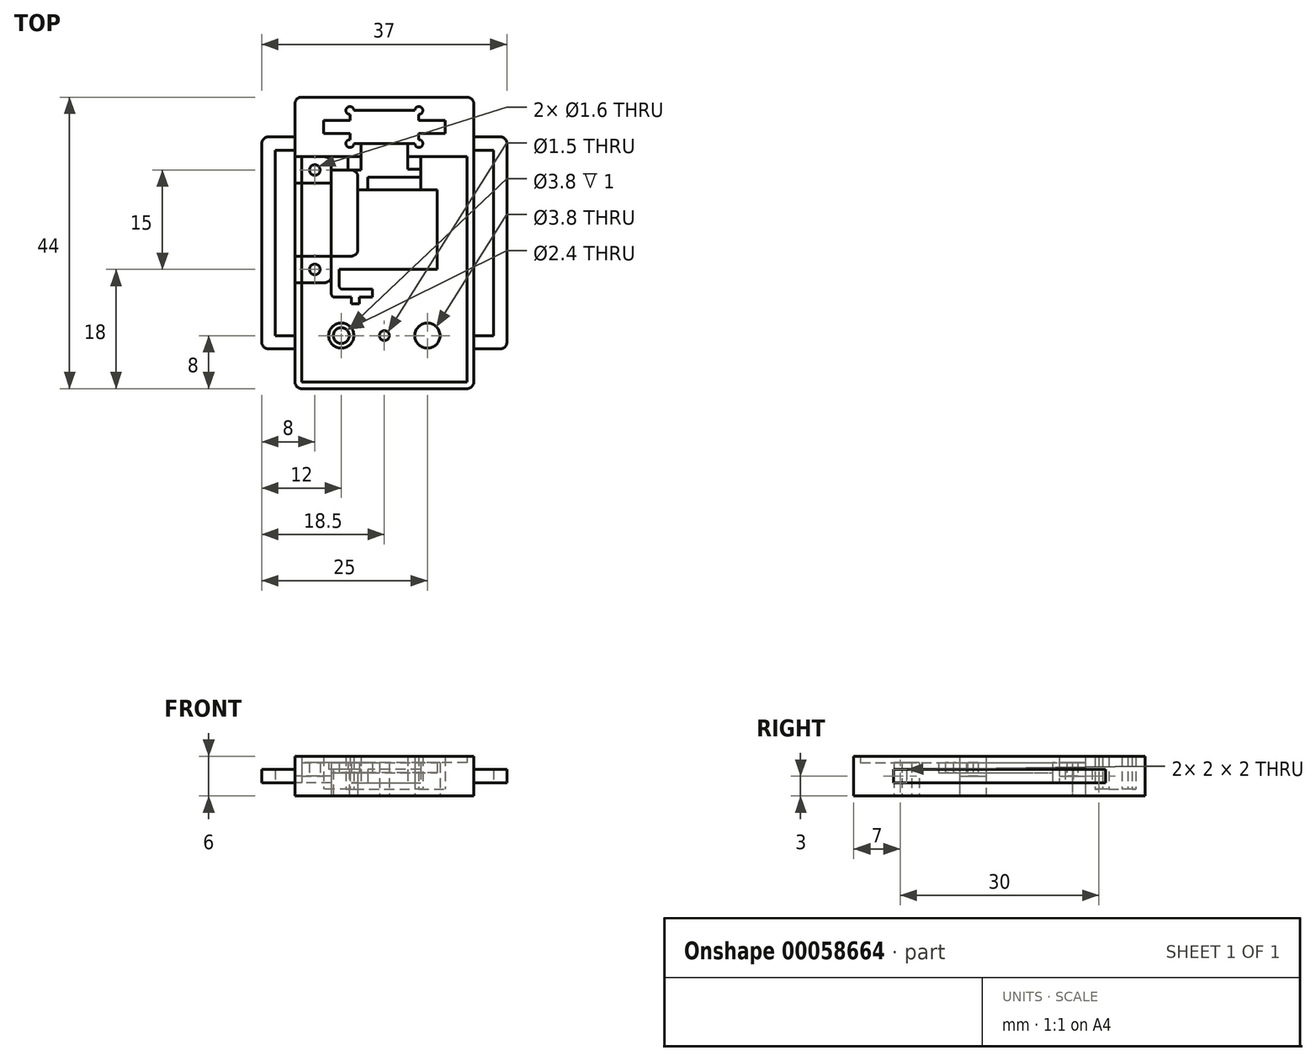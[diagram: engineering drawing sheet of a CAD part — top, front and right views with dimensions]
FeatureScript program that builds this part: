
annotation { "Feature Type Name" : "Feature", "Feature Type Description" : "" }
export const myFeature = defineFeature(function(context is Context, id is Id, definition is map)
    precondition{}
    {
        {
            var Q0;
            Q0=qCreatedBy(makeId("Top.planeOp"),FACE);
            var sketch = newSketch(context, id + "F0", { "sketchPlane" : qUnion([Q0])});
            skLineSegment(sketch, "E0", {"start": v(0, 0) * mm, "end": v(-12.5, 0) * mm});
            skLineSegment(sketch, "E1", {"start": v(-12.5, 0) * mm, "end": v(-12.5, 34) * mm});
            skLineSegment(sketch, "E2", {"start": v(-12.5, 34) * mm, "end": v(-9, 34) * mm});
            skCircle(sketch, "E3", {"center": v(-6.5, 7) * mm, "radius": 1.9 * mm});
            skCircle(sketch, "E4", {"center": v(0, 7) * mm, "radius": 0.75 * mm});
            skLineSegment(sketch, "E5", {"start": v(-8, 17) * mm, "end": v(0, 17) * mm});
            skLineSegment(sketch, "E6", {"start": v(-8, 29) * mm, "end": v(0, 29) * mm});
            skLineSegment(sketch, "E7", {"start": v(-4, 20) * mm, "end": v(-4, 29) * mm});
            skLineSegment(sketch, "E8", {"start": v(-8, 17) * mm, "end": v(-8, 29) * mm});
            skLineSegment(sketch, "E9", {"start": v(-12.5, 43) * mm, "end": v(0, 43) * mm});
            skLineSegment(sketch, "E10", {"start": v(-13.5, 42) * mm, "end": v(-13.5, 0) * mm});
            skLineSegment(sketch, "E11", {"start": v(-12.5, -1) * mm, "end": v(0, -1) * mm});
            skLineSegment(sketch, "E12.MirrorCS", {"start": v(12.5, 43) * mm, "end": v(0, 43) * mm});
            skLineSegment(sketch, "E13.MirrorCS", {"start": v(13.5, 42) * mm, "end": v(13.5, 0) * mm});
            skLineSegment(sketch, "E14.MirrorCS", {"start": v(12.5, 34) * mm, "end": v(0, 34) * mm});
            skLineSegment(sketch, "E15.MirrorCS", {"start": v(12.5, 0) * mm, "end": v(12.5, 34) * mm});
            skLineSegment(sketch, "E16.MirrorCS", {"start": v(0, 0) * mm, "end": v(12.5, 0) * mm});
            skLineSegment(sketch, "E17.MirrorCS", {"start": v(12.5, -1) * mm, "end": v(0, -1) * mm});
            skLineSegment(sketch, "E18.MirrorCS", {"start": v(8, 29) * mm, "end": v(0, 29) * mm});
            skLineSegment(sketch, "E19.MirrorCS", {"start": v(8, 17) * mm, "end": v(0, 17) * mm});
            skLineSegment(sketch, "E20.MirrorCS", {"start": v(8, 17) * mm, "end": v(8, 29) * mm});
            skLineSegment(sketch, "E21.MirrorCS", {"start": v(4, 17) * mm, "end": v(4, 29) * mm});
            skCircle(sketch, "E22.MirrorC", {"center": v(6.5, 7) * mm, "radius": 1.9 * mm});
            skLineSegment(sketch, "E23", {"start": v(0, 41) * mm, "end": v(-4.6, 41) * mm});
            skLineSegment(sketch, "E24", {"start": v(-5.2, 40.4) * mm, "end": v(-5.2, 36.6) * mm});
            skLineSegment(sketch, "E25", {"start": v(-4.6, 36) * mm, "end": v(0, 36) * mm});
            skLineSegment(sketch, "E26.MirrorCS", {"start": v(0, 41) * mm, "end": v(4.6, 41) * mm});
            skLineSegment(sketch, "E27.MirrorCS", {"start": v(5.2, 40.4) * mm, "end": v(5.2, 36.6) * mm});
            skLineSegment(sketch, "E28.MirrorCS", {"start": v(4.6, 36) * mm, "end": v(0, 36) * mm});
            skLineSegment(sketch, "E29", {"start": v(-8, 29) * mm, "end": v(-13.5, 29) * mm});
            skLineSegment(sketch, "E30", {"start": v(-8, 17) * mm, "end": v(-13.5, 17) * mm});
            skLineSegment(sketch, "E31.MirrorCS", {"start": v(8, 29) * mm, "end": v(13.5, 29) * mm});
            skLineSegment(sketch, "E32.MirrorCS", {"start": v(8, 17) * mm, "end": v(13.5, 17) * mm});
            skLineSegment(sketch, "E33", {"start": v(-3.5, 36) * mm, "end": v(-3.5, 29) * mm});
            skLineSegment(sketch, "E34.MirrorCS", {"start": v(3.5, 36) * mm, "end": v(3.5, 29) * mm});
            skArc(sketch, "E35", {"start": v(-4.6, 41) * mm, "mid": v(-5.62, 41.42) * mm, "end": v(-5.2, 40.4) * mm});
            skArc(sketch, "E36", {"start": v(-5.2, 36.6) * mm, "mid": v(-5.62, 35.58) * mm, "end": v(-4.6, 36) * mm});
            skArc(sketch, "E37.MirrorC", {"start": v(4.6, 41) * mm, "mid": v(5.62, 41.42) * mm, "end": v(5.2, 40.4) * mm});
            skArc(sketch, "E38.MirrorC", {"start": v(5.2, 36.6) * mm, "mid": v(5.62, 35.58) * mm, "end": v(4.6, 36) * mm});
            skLineSegment(sketch, "E39", {"start": v(-5, 19) * mm, "end": v(-13.5, 19) * mm});
            skLineSegment(sketch, "E40", {"start": v(-8, 17) * mm, "end": v(-8, 16) * mm});
            skLineSegment(sketch, "E41", {"start": v(-7.5, 12.8) * mm, "end": v(-5, 12.8) * mm});
            skLineSegment(sketch, "E42", {"start": v(-1.8, 12.8) * mm, "end": v(-1.8, 14) * mm});
            skLineSegment(sketch, "E43", {"start": v(-1.8, 14) * mm, "end": v(-6.3, 14) * mm});
            skLineSegment(sketch, "E44", {"start": v(-6.8, 14.5) * mm, "end": v(-6.8, 17) * mm});
            skLineSegment(sketch, "E45", {"start": v(-13.5, 5) * mm, "end": v(-17.5, 5) * mm});
            skLineSegment(sketch, "E46", {"start": v(-18.5, 6) * mm, "end": v(-18.5, 36) * mm});
            skLineSegment(sketch, "E47", {"start": v(-17.5, 37) * mm, "end": v(-13.5, 37) * mm});
            skLineSegment(sketch, "E48", {"start": v(-13.5, 7) * mm, "end": v(-16.5, 7) * mm});
            skLineSegment(sketch, "E49", {"start": v(-16.5, 7) * mm, "end": v(-16.5, 35) * mm});
            skLineSegment(sketch, "E50", {"start": v(-16.5, 35) * mm, "end": v(-13.5, 35) * mm});
            skLineSegment(sketch, "E51.MirrorCS", {"start": v(17.5, 37) * mm, "end": v(13.5, 37) * mm});
            skLineSegment(sketch, "E52.MirrorCS", {"start": v(16.5, 35) * mm, "end": v(13.5, 35) * mm});
            skLineSegment(sketch, "E53.MirrorCS", {"start": v(16.5, 7) * mm, "end": v(16.5, 35) * mm});
            skLineSegment(sketch, "E54.MirrorCS", {"start": v(13.5, 5) * mm, "end": v(17.5, 5) * mm});
            skLineSegment(sketch, "E55.MirrorCS", {"start": v(13.5, 7) * mm, "end": v(16.5, 7) * mm});
            skLineSegment(sketch, "E56.MirrorCS", {"start": v(18.5, 6) * mm, "end": v(18.5, 36) * mm});
            skPoint(sketch, "E57.visualSharp", {"position": v(-18.5, 37) * mm});
            skArc(sketch, "E57.filletArc", {"start": v(-17.5, 37) * mm, "mid": v(-18.2, 36.7) * mm, "end": v(-18.5, 36) * mm});
            skPoint(sketch, "E58.visualSharp", {"position": v(-18.5, 5) * mm});
            skArc(sketch, "E58.filletArc", {"start": v(-18.5, 6) * mm, "mid": v(-18.2, 5.3) * mm, "end": v(-17.5, 5) * mm});
            skPoint(sketch, "E59.visualSharp", {"position": v(18.5, 5) * mm});
            skArc(sketch, "E59.filletArc", {"start": v(17.5, 5) * mm, "mid": v(18.2, 5.3) * mm, "end": v(18.5, 6) * mm});
            skPoint(sketch, "E60.visualSharp", {"position": v(18.5, 37) * mm});
            skArc(sketch, "E60.filletArc", {"start": v(18.5, 36) * mm, "mid": v(18.2, 36.7) * mm, "end": v(17.5, 37) * mm});
            skPoint(sketch, "E61.visualSharp", {"position": v(13.5, 43) * mm});
            skArc(sketch, "E61.filletArc", {"start": v(13.5, 42) * mm, "mid": v(13.2, 42.7) * mm, "end": v(12.5, 43) * mm});
            skPoint(sketch, "E62.visualSharp", {"position": v(-13.5, 43) * mm});
            skArc(sketch, "E62.filletArc", {"start": v(-12.5, 43) * mm, "mid": v(-13.2, 42.7) * mm, "end": v(-13.5, 42) * mm});
            skPoint(sketch, "E63.visualSharp", {"position": v(-13.5, -1) * mm});
            skArc(sketch, "E63.filletArc", {"start": v(-13.5, 0) * mm, "mid": v(-13.2, -0.7) * mm, "end": v(-12.5, -1) * mm});
            skPoint(sketch, "E64.visualSharp", {"position": v(13.5, -1) * mm});
            skArc(sketch, "E64.filletArc", {"start": v(12.5, -1) * mm, "mid": v(13.2, -0.7) * mm, "end": v(13.5, 0) * mm});
            skLineSegment(sketch, "E65", {"start": v(-5, 12.8) * mm, "end": v(-5, 11.8) * mm});
            skLineSegment(sketch, "E66", {"start": v(-5, 11.8) * mm, "end": v(-3.8, 11.8) * mm});
            skLineSegment(sketch, "E67", {"start": v(-3.8, 11.8) * mm, "end": v(-3.8, 12.8) * mm});
            skLineSegment(sketch, "E68.trimOffspring", {"start": v(-3.8, 12.8) * mm, "end": v(-1.8, 12.8) * mm});
            skLineSegment(sketch, "E69", {"start": v(5.5, 34) * mm, "end": v(5.5, 29) * mm});
            skLineSegment(sketch, "E70", {"start": v(3.5, 32.1) * mm, "end": v(5.5, 32.1) * mm});
            skLineSegment(sketch, "E71", {"start": v(3.5, 30.9) * mm, "end": v(5.5, 30.9) * mm});
            skCircle(sketch, "E72", {"center": v(-6.5, 7) * mm, "radius": 1.2 * mm});
            skCircle(sketch, "E73.MirrorC", {"center": v(6.5, 7) * mm, "radius": 1.2 * mm});
            skPoint(sketch, "E74.visualSharp", {"position": v(-6.8, 14) * mm});
            skArc(sketch, "E74.filletArc", {"start": v(-6.8, 14.5) * mm, "mid": v(-6.65, 14.15) * mm, "end": v(-6.3, 14) * mm});
            skPoint(sketch, "E75.visualSharp", {"position": v(-8, 12.8) * mm});
            skArc(sketch, "E75.filletArc", {"start": v(-8, 13.3) * mm, "mid": v(-7.85, 12.95) * mm, "end": v(-7.5, 12.8) * mm});
            skLineSegment(sketch, "E76", {"start": v(3.5, 30.9) * mm, "end": v(-3.5, 30.9) * mm});
            skLineSegment(sketch, "E77", {"start": v(-8, 29) * mm, "end": v(-8, 33) * mm});
            skLineSegment(sketch, "E78", {"start": v(-12.5, 34) * mm, "end": v(-13.5, 34) * mm});
            skLineSegment(sketch, "E79", {"start": v(-4, 29) * mm, "end": v(-4, 30.9) * mm});
            skCircle(sketch, "E80", {"center": v(-10.5, 32) * mm, "radius": 1.75 * mm});
            skCircle(sketch, "E81", {"center": v(-10.5, 32) * mm, "radius": 0.8 * mm});
            skLineSegment(sketch, "E82", {"start": v(-8, 30) * mm, "end": v(-13.5, 30) * mm});
            skLineSegment(sketch, "E83", {"start": v(-9, 15) * mm, "end": v(-13.5, 15) * mm});
            skCircle(sketch, "E84", {"center": v(-10.5, 17) * mm, "radius": 0.8 * mm});
            skCircle(sketch, "E85", {"center": v(-10.5, 17) * mm, "radius": 1.75 * mm});
            skLineSegment(sketch, "E86.bottom", {"start": v(-5.2, 37.5) * mm, "end": v(-9.2, 37.5) * mm});
            skLineSegment(sketch, "E86.top", {"start": v(-5.2, 39.5) * mm, "end": v(-9.2, 39.5) * mm});
            skLineSegment(sketch, "E86.left", {"start": v(-5.2, 37.5) * mm, "end": v(-5.2, 39.5) * mm});
            skLineSegment(sketch, "E86.right", {"start": v(-9.2, 37.5) * mm, "end": v(-9.2, 39.5) * mm});
            skLineSegment(sketch, "E87.MirrorCS", {"start": v(5.2, 39.5) * mm, "end": v(9.2, 39.5) * mm});
            skLineSegment(sketch, "E88.MirrorCS", {"start": v(9.2, 37.5) * mm, "end": v(9.2, 39.5) * mm});
            skLineSegment(sketch, "E89.MirrorCS", {"start": v(5.2, 37.5) * mm, "end": v(9.2, 37.5) * mm});
            skArc(sketch, "E90.filletArc", {"start": v(-9, 15) * mm, "mid": v(-8.3, 15.3) * mm, "end": v(-8, 16) * mm});
            skPoint(sketch, "E91.newPointA", {"position": v(0, 34) * mm});
            skArc(sketch, "E91.filletArc", {"start": v(-8, 33) * mm, "mid": v(-8.3, 33.7) * mm, "end": v(-9, 34) * mm});
            skPoint(sketch, "E92.newPointB", {"position": v(-4, 17) * mm});
            skArc(sketch, "E92.filletArc", {"start": v(-5, 19) * mm, "mid": v(-4.3, 19.3) * mm, "end": v(-4, 20) * mm});
            skLineSegment(sketch, "E93", {"start": v(-4, 30.9) * mm, "end": v(-4, 31) * mm});
            skLineSegment(sketch, "E94", {"start": v(-5, 32) * mm, "end": v(-8, 32) * mm});
            skPoint(sketch, "E95.visualSharp", {"position": v(-4, 32) * mm});
            skArc(sketch, "E95.filletArc", {"start": v(-4, 31) * mm, "mid": v(-4.3, 31.7) * mm, "end": v(-5, 32) * mm});
            skLineSegment(sketch, "E96", {"start": v(-5, 32) * mm, "end": v(-3.5, 32) * mm});
            skLineSegment(sketch, "E97", {"start": v(-2.5, 30.9) * mm, "end": v(-2.5, 29) * mm});
            skLineSegment(sketch, "E98.bottom", {"start": v(-3.5, 32) * mm, "end": v(-5.5, 32) * mm});
            skLineSegment(sketch, "E98.top", {"start": v(-3.5, 34) * mm, "end": v(-5.5, 34) * mm});
            skLineSegment(sketch, "E98.left", {"start": v(-3.5, 32) * mm, "end": v(-3.5, 34) * mm});
            skLineSegment(sketch, "E98.right", {"start": v(-5.5, 32) * mm, "end": v(-5.5, 34) * mm});
            skLineSegment(sketch, "E99", {"start": v(-5.5, 34) * mm, "end": v(-9, 34) * mm});
            skLineSegment(sketch, "E100", {"start": v(-8, 13.3) * mm, "end": v(-8, 17) * mm});
            skSolve(sketch);
        }
        {
            var Q0;
            {var subQ18=sQuery(id+"F0.wireOp",EDGE,"E9");Q0=makeQuery(id+"F0.imprint","IMPRINT",FACE,{"disambiguationData":[TD([[makeQuery(id+"F0.imprint","IMPRINT",EDGE,{"derivedFrom":subQ18}),-1.0]])]});}
            var Q1;
            {var subQ7=sQuery(id+"F0.wireOp",EDGE,"E0");Q1=makeQuery(id+"F0.imprint","IMPRINT",FACE,{"disambiguationData":[TD([[makeQuery(id+"F0.imprint","IMPRINT",EDGE,{"derivedFrom":subQ7}),1.0]])]});}
            var Q2;
            {var subQ0=sQuery(id+"F0.wireOp",EDGE,"E31.MirrorCS");var subQ3=sQuery(id+"F0.wireOp",EDGE,"E13.MirrorCS");var subQ4=makeQuery(id+"F0.imprint","INTERSECT",VERTEX,{"derivedFrom":[subQ3,subQ0]});Q2=makeQuery(id+"F0.imprint","IMPRINT",FACE,{"disambiguationData":[TD([[makeQuery(id+"F0.imprint","IMPRINT",EDGE,{"disambiguationData":[TD([[subQ4,-1.0]])],"derivedFrom":subQ3}),-1.0]])]});}
            extrude(context, id + "F1", {"entities" : qUnion([Q0, Q1, Q2]), "depth" : 6 * mm});
        }
        {
            var Q0;
            {var subQ1=sQuery(id+"F0.wireOp",EDGE,"E14.MirrorCS");var subQ6=sQuery(id+"F0.wireOp",EDGE,"E15.MirrorCS");var subQ9=makeQuery(id+"F0.imprint","INTERSECT",VERTEX,{"derivedFrom":[subQ1,subQ6]});Q0=makeQuery(id+"F0.imprint","IMPRINT",FACE,{"disambiguationData":[TD([[makeQuery(id+"F0.imprint","IMPRINT",EDGE,{"disambiguationData":[TD([[subQ9,-1.0]])],"derivedFrom":subQ1}),1.0]])]});}
            var Q1;
            {var subQ3=sQuery(id+"F0.wireOp",EDGE,"E20.MirrorCS");Q1=makeQuery(id+"F0.imprint","IMPRINT",FACE,{"disambiguationData":[TD([[makeQuery(id+"F0.imprint","IMPRINT",EDGE,{"derivedFrom":subQ3}),-1.0]])]});}
            var Q2;
            {var subQ10=sQuery(id+"F0.wireOp",EDGE,"E0");Q2=makeQuery(id+"F0.imprint","IMPRINT",FACE,{"disambiguationData":[TD([[makeQuery(id+"F0.imprint","IMPRINT",EDGE,{"derivedFrom":subQ10}),-1.0]])]});}
            var Q3;
            {var subQ1=sQuery(id+"F0.wireOp",EDGE,"E91.filletArc");Q3=makeQuery(id+"F0.imprint","IMPRINT",FACE,{"disambiguationData":[TD([[makeQuery(id+"F0.imprint","IMPRINT",EDGE,{"derivedFrom":subQ1}),-1.0]])]});}
            extrude(context, id + "F2", {"entities" : qUnion([Q0, Q1, Q2, Q3]), "operationType" : NewBodyOperationType.ADD, "depth" : 5 * mm});
        }
        {
            var Q0;
            {var subQ6=sQuery(id+"F0.wireOp",EDGE,"E7");Q0=makeQuery(id+"F0.imprint","IMPRINT",FACE,{"disambiguationData":[TD([[makeQuery(id+"F0.imprint","IMPRINT",EDGE,{"derivedFrom":subQ6}),-1.0]])]});}
            var Q1;
            {var subQ2=sQuery(id+"F0.wireOp",EDGE,"E20.MirrorCS");Q1=makeQuery(id+"F0.imprint","IMPRINT",FACE,{"disambiguationData":[TD([[makeQuery(id+"F0.imprint","IMPRINT",EDGE,{"derivedFrom":subQ2}),1.0]])]});}
            var Q2;
            {var subQ2=sQuery(id+"F0.wireOp",EDGE,"E40");Q2=makeQuery(id+"F0.imprint","IMPRINT",FACE,{"disambiguationData":[TD([[makeQuery(id+"F0.imprint","IMPRINT",EDGE,{"derivedFrom":subQ2}),1.0]])]});}
            var Q3;
            Q3=makeQuery(id+"F0.imprint","IMPRINT",FACE,{"disambiguationData":[TD([[makeQuery(id+"F0.imprint","IMPRINT",EDGE,{"derivedFrom":sQuery(id+"F0.wireOp",EDGE,"E41")}),1.0]])]});
            extrude(context, id + "F3", {"entities" : qUnion([Q0, Q1, Q2, Q3]), "operationType" : NewBodyOperationType.ADD, "depth" : 3.5 * mm});
        }
        {
            var Q0;
            {var subQ0=sQuery(id+"F0.wireOp",EDGE,"E39");var subQ3=sQuery(id+"F0.wireOp",EDGE,"E1");var subQ4=makeQuery(id+"F0.imprint","INTERSECT",VERTEX,{"derivedFrom":[subQ3,subQ0]});Q0=makeQuery(id+"F0.imprint","IMPRINT",FACE,{"disambiguationData":[TD([[makeQuery(id+"F0.imprint","IMPRINT",EDGE,{"disambiguationData":[TD([[subQ4,-1.0]])],"derivedFrom":subQ3}),-1.0]])]});}
            var Q1;
            {var subQ3=sQuery(id+"F0.wireOp",EDGE,"f297b26b-06aa-41ef-a3ca-324e2ecd0da6");Q1=makeQuery(id+"F0.imprint","IMPRINT",FACE,{"disambiguationData":[TD([[makeQuery(id+"F0.imprint","IMPRINT",EDGE,{"derivedFrom":subQ3}),1.0]])]});}
            var Q2;
            {var subQ0=sQuery(id+"F0.wireOp",EDGE,"E29");var subQ1=sQuery(id+"F0.wireOp",EDGE,"E1");var subQ2=makeQuery(id+"F0.imprint","INTERSECT",VERTEX,{"derivedFrom":[subQ1,subQ0]});Q2=makeQuery(id+"F0.imprint","IMPRINT",FACE,{"disambiguationData":[TD([[makeQuery(id+"F0.imprint","IMPRINT",EDGE,{"disambiguationData":[TD([[subQ2,-1.0]])],"derivedFrom":subQ1}),-1.0]])]});}
            extrude(context, id + "F4", {"entities" : qUnion([Q0, Q1, Q2]), "depth" : 5 * mm, "hasSecondDirection" : true, "secondDirectionOppositeDirection" : false, "secondDirectionDepth" : 2 * mm});
        }
        {
            var Q0;
            {var subQ0=sQuery(id+"F0.wireOp",EDGE,"E29");var subQ1=sQuery(id+"F0.wireOp",EDGE,"E1");var subQ2=makeQuery(id+"F0.imprint","INTERSECT",VERTEX,{"derivedFrom":[subQ1,subQ0]});Q0=makeQuery(id+"F0.imprint","IMPRINT",FACE,{"disambiguationData":[TD([[makeQuery(id+"F0.imprint","IMPRINT",EDGE,{"disambiguationData":[TD([[subQ2,-1.0]])],"derivedFrom":subQ1}),1.0]])]});}
            var Q1;
            {var subQ0=sQuery(id+"F0.wireOp",EDGE,"E39");var subQ1=sQuery(id+"F0.wireOp",EDGE,"E1");var subQ2=makeQuery(id+"F0.imprint","INTERSECT",VERTEX,{"derivedFrom":[subQ1,subQ0]});Q1=makeQuery(id+"F0.imprint","IMPRINT",FACE,{"disambiguationData":[TD([[makeQuery(id+"F0.imprint","IMPRINT",EDGE,{"disambiguationData":[TD([[subQ2,-1.0]])],"derivedFrom":subQ1}),1.0]])]});}
            extrude(context, id + "F5", {"entities" : qUnion([Q0, Q1]), "depth" : 6 * mm, "hasSecondDirection" : true, "secondDirectionOppositeDirection" : false, "secondDirectionDepth" : 2 * mm});
        }
        {
            var Q0;
            Q0=makeQuery(id+"F0.imprint","IMPRINT",FACE,{"disambiguationData":[TD([[makeQuery(id+"F0.imprint","IMPRINT",EDGE,{"derivedFrom":sQuery(id+"F0.wireOp",EDGE,"E23")}),1.0]])]});
            var Q1;
            Q1=makeQuery(id+"F0.imprint","IMPRINT",FACE,{"disambiguationData":[TD([[makeQuery(id+"F0.imprint","IMPRINT",EDGE,{"derivedFrom":sQuery(id+"F0.wireOp",EDGE,"E86.bottom")}),-1.0]])]});
            var Q2;
            {var subQ0=sQuery(id+"F0.wireOp",EDGE,"E87.MirrorCS");Q2=makeQuery(id+"F0.imprint","IMPRINT",FACE,{"disambiguationData":[TD([[makeQuery(id+"F0.imprint","IMPRINT",EDGE,{"derivedFrom":subQ0}),-1.0]])]});}
            extrude(context, id + "F6", {"entities" : qUnion([Q0, Q1, Q2]), "operationType" : NewBodyOperationType.ADD, "depth" : 1 * mm});
        }
        {
            var Q0;
            {var subQ7=sQuery(id+"F0.wireOp",EDGE,"E14.MirrorCS");var subQ8=sQuery(id+"F0.wireOp",EDGE,"E2");var subQ9=makeQuery(id+"F0.imprint","INTERSECT",VERTEX,{"derivedFrom":[subQ8,subQ7]});Q0=makeQuery(id+"F0.imprint","IMPRINT",FACE,{"disambiguationData":[TD([[makeQuery(id+"F0.imprint","IMPRINT",EDGE,{"disambiguationData":[TD([[subQ9,1.0]])],"derivedFrom":subQ8}),1.0]])]});}
            var Q1;
            {var subQ0=sQuery(id+"F0.wireOp",EDGE,"E70");Q1=makeQuery(id+"F0.imprint","IMPRINT",FACE,{"disambiguationData":[TD([[makeQuery(id+"F0.imprint","IMPRINT",EDGE,{"derivedFrom":subQ0}),-1.0]])]});}
            var Q2;
            {var subQ0=sQuery(id+"F0.wireOp",EDGE,"E76");Q2=makeQuery(id+"F0.imprint","IMPRINT",FACE,{"disambiguationData":[TD([[makeQuery(id+"F0.imprint","IMPRINT",EDGE,{"derivedFrom":subQ0}),-1.0]])]});}
            var Q3;
            {var subQ0=sQuery(id+"F0.wireOp",EDGE,"pBWgLYAh-YtHk-MjLS-udOA-cUkfiK7Ams3F");Q3=makeQuery(id+"F0.imprint","IMPRINT",FACE,{"disambiguationData":[TD([[makeQuery(id+"F0.imprint","IMPRINT",EDGE,{"derivedFrom":subQ0}),-1.0]])]});}
            var Q4;
            {var subQ5=sQuery(id+"F0.wireOp",EDGE,"pBWgLYAh-YtHk-MjLS-udOA-cUkfiK7Ams3F");Q4=makeQuery(id+"F0.imprint","IMPRINT",FACE,{"disambiguationData":[TD([[makeQuery(id+"F0.imprint","IMPRINT",EDGE,{"derivedFrom":subQ5}),1.0]])]});}
            var Q5;
            {var subQ0=sQuery(id+"F0.wireOp",EDGE,"E79");Q5=makeQuery(id+"F0.imprint","IMPRINT",FACE,{"disambiguationData":[TD([[makeQuery(id+"F0.imprint","IMPRINT",EDGE,{"derivedFrom":subQ0}),-1.0]])]});}
            var Q6;
            {var subQ3=sQuery(id+"F0.wireOp",EDGE,"E97");Q6=makeQuery(id+"F0.imprint","IMPRINT",FACE,{"disambiguationData":[TD([[makeQuery(id+"F0.imprint","IMPRINT",EDGE,{"derivedFrom":subQ3}),-1.0]])]});}
            extrude(context, id + "F7", {"entities" : qUnion([Q0, Q1, Q2, Q3, Q4, Q5, Q6]), "operationType" : NewBodyOperationType.ADD, "depth" : 2 * mm});
        }
        {
            var Q0;
            {var subQ4=sQuery(id+"F0.wireOp",EDGE,"E45");Q0=makeQuery(id+"F0.imprint","IMPRINT",FACE,{"disambiguationData":[TD([[makeQuery(id+"F0.imprint","IMPRINT",EDGE,{"derivedFrom":subQ4}),-1.0]])]});}
            var Q1;
            {var subQ4=sQuery(id+"F0.wireOp",EDGE,"E51.MirrorCS");Q1=makeQuery(id+"F0.imprint","IMPRINT",FACE,{"disambiguationData":[TD([[makeQuery(id+"F0.imprint","IMPRINT",EDGE,{"derivedFrom":subQ4}),1.0]])]});}
            extrude(context, id + "F8", {"entities" : qUnion([Q0, Q1]), "operationType" : NewBodyOperationType.ADD, "depth" : 4 * mm, "hasSecondDirection" : true, "secondDirectionOppositeDirection" : false, "secondDirectionDepth" : 2 * mm});
        }
        {
            var Q0;
            {var subQ5=sQuery(id+"F0.wireOp",EDGE,"E70");Q0=makeQuery(id+"F0.imprint","IMPRINT",FACE,{"disambiguationData":[TD([[makeQuery(id+"F0.imprint","IMPRINT",EDGE,{"derivedFrom":subQ5}),1.0]])]});}
            var Q1;
            {var subQ3=sQuery(id+"F0.wireOp",EDGE,"E71");Q1=makeQuery(id+"F0.imprint","IMPRINT",FACE,{"disambiguationData":[TD([[makeQuery(id+"F0.imprint","IMPRINT",EDGE,{"derivedFrom":subQ3}),-1.0]])]});}
            var Q2;
            {var subQ3=sQuery(id+"F0.wireOp",EDGE,"E97");Q2=makeQuery(id+"F0.imprint","IMPRINT",FACE,{"disambiguationData":[TD([[makeQuery(id+"F0.imprint","IMPRINT",EDGE,{"derivedFrom":subQ3}),1.0]])]});}
            var Q3;
            Q3=makeQuery(id+"F0.imprint","IMPRINT",FACE,{"disambiguationData":[TD([[makeQuery(id+"F0.imprint","IMPRINT",EDGE,{"derivedFrom":sQuery(id+"F0.wireOp",EDGE,"E98.top")}),1.0]])]});
            extrude(context, id + "F9", {"entities" : qUnion([Q0, Q1, Q2, Q3]), "operationType" : NewBodyOperationType.ADD, "depth" : 4 * mm});
        }
        {
            var Q0;
            Q0=makeQuery(id+"F0.imprint","IMPRINT",FACE,{"disambiguationData":[TD([[makeQuery(id+"F0.imprint","IMPRINT",EDGE,{"derivedFrom":sQuery(id+"F0.wireOp",EDGE,"E22.MirrorC")}),-1.0]])]});
            var Q1;
            Q1=makeQuery(id+"F0.imprint","IMPRINT",FACE,{"disambiguationData":[TD([[makeQuery(id+"F0.imprint","IMPRINT",EDGE,{"derivedFrom":sQuery(id+"F0.wireOp",EDGE,"E3")}),1.0]])]});
            extrude(context, id + "F10", {"entities" : qUnion([Q0, Q1]), "operationType" : NewBodyOperationType.ADD, "depth" : 4 * mm});
        }
        {
            var Q0;
            {var subQ5=sQuery(id+"F0.wireOp",EDGE,"E2");Q0=makeQuery(id+"F0.imprint","IMPRINT",FACE,{"disambiguationData":[TD([[makeQuery(id+"F0.imprint","IMPRINT",EDGE,{"derivedFrom":subQ5}),-1.0]])]});}
            var Q1;
            Q1=makeQuery(id+"F0.imprint","IMPRINT",FACE,{"disambiguationData":[TD([[makeQuery(id+"F0.imprint","IMPRINT",EDGE,{"derivedFrom":sQuery(id+"F0.wireOp",EDGE,"E80")}),1.0]])]});
            var Q2;
            {var subQ0=sQuery(id+"F0.wireOp",EDGE,"E30");var subQ1=sQuery(id+"F0.wireOp",EDGE,"E1");var subQ2=makeQuery(id+"F0.imprint","INTERSECT",VERTEX,{"derivedFrom":[subQ1,subQ0]});Q2=makeQuery(id+"F0.imprint","IMPRINT",FACE,{"disambiguationData":[TD([[makeQuery(id+"F0.imprint","IMPRINT",EDGE,{"disambiguationData":[TD([[subQ2,-1.0]])],"derivedFrom":subQ1}),-1.0]])]});}
            var Q3;
            {var subQ0=sQuery(id+"F0.wireOp",EDGE,"E40");Q3=makeQuery(id+"F0.imprint","IMPRINT",FACE,{"disambiguationData":[TD([[makeQuery(id+"F0.imprint","IMPRINT",EDGE,{"derivedFrom":subQ0}),-1.0]])]});}
            var Q4;
            {var subQ0=sQuery(id+"F0.wireOp",EDGE,"E85");var subQ1=sQuery(id+"F0.wireOp",EDGE,"E30");var subQ2=makeQuery(id+"F0.imprint","INTERSECT",VERTEX,{"disambiguationData":[OD(0.0)],"derivedFrom":[subQ1,subQ0]});Q4=makeQuery(id+"F0.imprint","IMPRINT",FACE,{"disambiguationData":[TD([[makeQuery(id+"F0.imprint","IMPRINT",EDGE,{"disambiguationData":[TD([[subQ2,-1.0]])],"derivedFrom":subQ1}),1.0]])]});}
            var Q5;
            {var subQ0=sQuery(id+"F0.wireOp",EDGE,"E85");var subQ1=sQuery(id+"F0.wireOp",EDGE,"E30");var subQ2=makeQuery(id+"F0.imprint","INTERSECT",VERTEX,{"disambiguationData":[OD(0.0)],"derivedFrom":[subQ1,subQ0]});Q5=makeQuery(id+"F0.imprint","IMPRINT",FACE,{"disambiguationData":[TD([[makeQuery(id+"F0.imprint","IMPRINT",EDGE,{"disambiguationData":[TD([[subQ2,-1.0]])],"derivedFrom":subQ1}),-1.0]])]});}
            var Q6;
            {var subQ0=sQuery(id+"F0.wireOp",EDGE,"E90.filletArc");Q6=makeQuery(id+"F0.imprint","IMPRINT",FACE,{"disambiguationData":[TD([[makeQuery(id+"F0.imprint","IMPRINT",EDGE,{"derivedFrom":subQ0}),1.0]])]});}
            extrude(context, id + "F11", {"entities" : qUnion([Q0, Q1, Q2, Q3, Q4, Q5, Q6]), "depth" : 5 * mm, "hasSecondDirection" : true, "secondDirectionOppositeDirection" : false, "secondDirectionDepth" : 3 * mm});
        }
        {
            var Q0;
            {var subQ0=sQuery(id+"F0.wireOp",EDGE,"E78");Q0=makeQuery(id+"F0.imprint","IMPRINT",FACE,{"disambiguationData":[TD([[makeQuery(id+"F0.imprint","IMPRINT",EDGE,{"derivedFrom":subQ0}),1.0]])]});}
            var Q1;
            {var subQ0=sQuery(id+"F0.wireOp",EDGE,"E30");var subQ1=sQuery(id+"F0.wireOp",EDGE,"E1");var subQ2=makeQuery(id+"F0.imprint","INTERSECT",VERTEX,{"derivedFrom":[subQ1,subQ0]});Q1=makeQuery(id+"F0.imprint","IMPRINT",FACE,{"disambiguationData":[TD([[makeQuery(id+"F0.imprint","IMPRINT",EDGE,{"disambiguationData":[TD([[subQ2,-1.0]])],"derivedFrom":subQ1}),1.0]])]});}
            var Q2;
            {var subQ0=sQuery(id+"F0.wireOp",EDGE,"E83");var subQ1=sQuery(id+"F0.wireOp",EDGE,"E1");var subQ2=makeQuery(id+"F0.imprint","INTERSECT",VERTEX,{"derivedFrom":[subQ1,subQ0]});Q2=makeQuery(id+"F0.imprint","IMPRINT",FACE,{"disambiguationData":[TD([[makeQuery(id+"F0.imprint","IMPRINT",EDGE,{"disambiguationData":[TD([[subQ2,-1.0]])],"derivedFrom":subQ1}),1.0]])]});}
            extrude(context, id + "F12", {"entities" : qUnion([Q0, Q1, Q2]), "depth" : 6 * mm, "hasSecondDirection" : true, "secondDirectionOppositeDirection" : false, "secondDirectionDepth" : 3 * mm});
        }
    });
